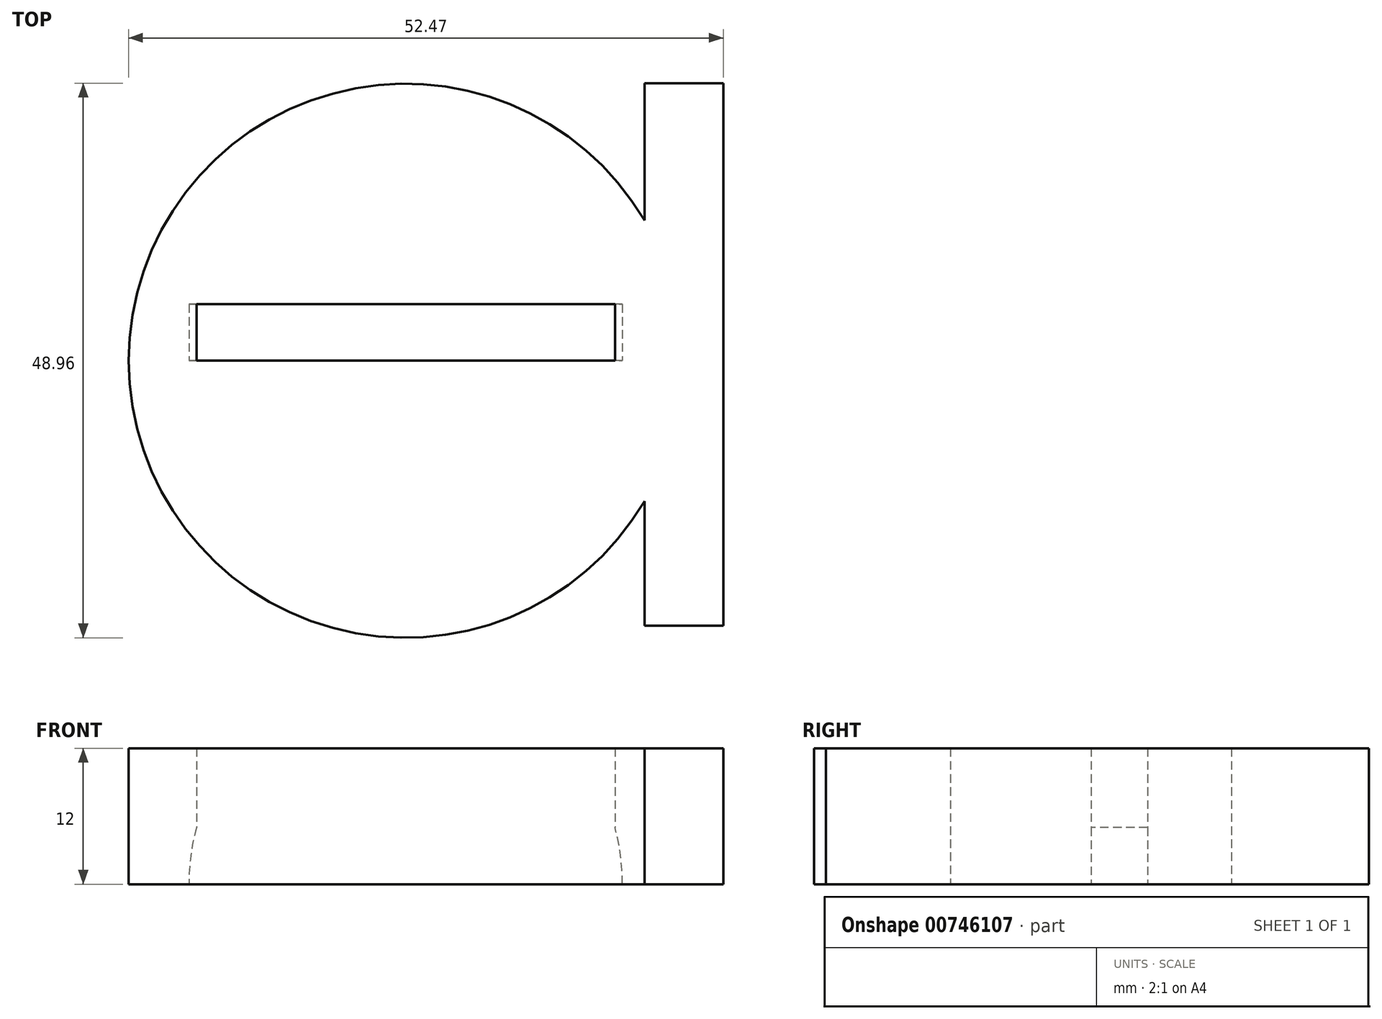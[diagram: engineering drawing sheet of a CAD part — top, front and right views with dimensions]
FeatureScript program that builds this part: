
annotation { "Feature Type Name" : "Feature", "Feature Type Description" : "" }
export const myFeature = defineFeature(function(context is Context, id is Id, definition is map)
    precondition{}
    {
        {
            var Q0;
            Q0=qCreatedBy(makeId("Top.planeOp"),FACE);
            var sketch = newSketch(context, id + "F0", { "sketchPlane" : qUnion([Q0])});
            skCircle(sketch, "E0", {"center": v(0, 0) * mm, "radius": 24.45 * mm});
            skSolve(sketch);
        }
        {
            var Q0;
            Q0 = qSketchRegion(id + "F0", true);
            extrude(context, id + "F1", {"entities" : qUnion([Q0]), "depth" : 5 * mm, "offsetDistance" : 25.4 * mm});
        }
        {
            var Q0;
            Q0=qCreatedBy(makeId("Front.planeOp"),FACE);
            var sketch = newSketch(context, id + "F2", { "sketchPlane" : qUnion([Q0])});
            skCircle(sketch, "E1", {"center": v(0, 0) * mm, "radius": 19.13 * mm});
            skSolve(sketch);
        }
        {
            var Q0;
            Q0=makeQuery(id+"F2.imprint","IMPRINT",FACE,{"disambiguationData":[TD([[makeQuery(id+"F2.imprint","IMPRINT",EDGE,{"derivedFrom":sQuery(id+"F2.wireOp",EDGE,"E1")}),1.0]])]});
            extrude(context, id + "F3", {"entities" : qUnion([Q0]), "operationType" : NewBodyOperationType.REMOVE, "oppositeDirection" : true, "depth" : 5 * mm, "offsetDistance" : 25.4 * mm});
        }
        {
            var Q0;
            Q0=qCreatedBy(makeId("Top.planeOp"),FACE);
            var sketch = newSketch(context, id + "F4", { "sketchPlane" : qUnion([Q0])});
            skLineSegment(sketch, "E2.bottom", {"start": v(21.07, 24.5) * mm, "end": v(28.02, 24.5) * mm});
            skLineSegment(sketch, "E2.top", {"start": v(21.07, -23.4) * mm, "end": v(28.02, -23.4) * mm});
            skLineSegment(sketch, "E2.left", {"start": v(21.07, 24.5) * mm, "end": v(21.07, -23.4) * mm});
            skLineSegment(sketch, "E2.right", {"start": v(28.02, 24.5) * mm, "end": v(28.02, -23.4) * mm});
            skSolve(sketch);
        }
        {
            var Q0;
            Q0=makeQuery(id+"F4.imprint","IMPRINT",FACE,{"disambiguationData":[TD([[makeQuery(id+"F4.imprint","IMPRINT",EDGE,{"derivedFrom":sQuery(id+"F4.wireOp",EDGE,"E2.bottom")}),-1.0]])]});
            extrude(context, id + "F5", {"entities" : qUnion([Q0]), "operationType" : NewBodyOperationType.ADD, "depth" : 5 * mm, "offsetDistance" : 25.4 * mm});
        }
        {
            var Q0;
            Q0=makeQuery(id+"F5.boolean.opBoolean","MERGE",FACE,{"derivedFrom":[makeQuery(id+"F1.opExtrude","CAP_FACE",FACE,{"disambiguationData":[OSD([sQuery(id+"F0.wireOp",EDGE,"E0")])],"isStart":false}),makeQuery(id+"F5.opExtrude","CAP_FACE",FACE,{"disambiguationData":[OSD([sQuery(id+"F4.wireOp",EDGE,"E2.bottom"),sQuery(id+"F4.wireOp",EDGE,"E2.top"),sQuery(id+"F4.wireOp",EDGE,"E2.left"),sQuery(id+"F4.wireOp",EDGE,"E2.right")])],"isStart":false})]});
            extrude(context, id + "F6", {"entities" : qUnion([Q0]), "operationType" : NewBodyOperationType.ADD, "depth" : 7 * mm, "offsetDistance" : 25.4 * mm});
        }
    });
